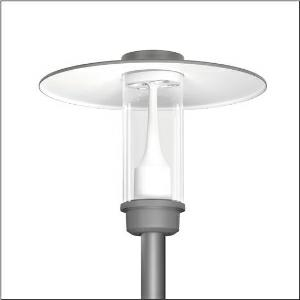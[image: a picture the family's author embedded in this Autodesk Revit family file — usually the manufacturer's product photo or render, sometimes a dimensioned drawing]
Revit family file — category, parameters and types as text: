
# Revit family: litepole_2_iq___p1_0a_5xa5425ff14h_a7e5
name_source: partatom
category: Lighting Fixtures
units: mm (PartAtom-declared; Revit-internal decimal feet)

## family parameters
Cut with Voids When Loaded = No
Host = Face
Light Source = No
Part Type = Normal
Room Calculation Point = No
Round Connector Dimension = Use Diameter
Shared = No

## types (1)
- --- (1 x LED, 1520 lm, 10.5 W, 3000K)
    Apparent Load = 11 VA
    CIE Flux Codes = 33 62 89 96 100
    Color Rendering = 70
    Color Temperature = 3000K
    Default Elevation = 1800 mm
    Description = Litepole 2 iQ, mast luminaire, Module 540 iQ-SR, primary light control with 3 zone facetted reflector, of plastic, silver coated, highly specular, structured, primary optical cover: cover, of PMMA, transparent, light distribution: P1.0a, light emission: direct distribution, primary light characteristic: strongly asymmetric, installation type: post-top, LED, High Power LED, rated luminous flux: 1.520lm, luminous efficacy: 145lm/W, light colour: 730, colour temperature: 3000K, control gear: iQ Street-Remote, control: Auto-Match, Temp-Guard, Lumen-Switch, Night-Set, Smart-Wire, Light-Fading, Desk-Remote (wireless, voltage-free reading and setting of iQ features in the workshop via application-optimized NFC function/RFID function), optimised constant luminous flux control (CLO 2.0), Street-Remote, pre-setting: logarithmic dimming characteristic, with terminal, 6-pole, max. 2.5mm², mains connection: 230..240V, AC, 50/60Hz, start of lifetime: 11W, end of service life: 11W, reduction: 5W, luminaire housing, upper part, of aluminium, coated, Siteco® metallic grey (DB 702S), diameter: 750mm, height: 590mm, spigot size: d x l = 76 x 70mm (post-top) | with reducer (optional accessory) 60 x 70mm, mounting height: 3..5m, post-top mast mounting element, of diecast aluminium, coated, Siteco® metallic grey (DB 702S), Module 540 iQ-SR, traffic white (RAL 9016), equipment: standard, protection rating (complete): IP65, insulation class (complete): insulation class II (safety insulation), certification: CE, ENEC, VDE, packaging unit: 1 piece

Light Distribution: P1.0a
    Height = 590 mm
    Lamp = 1 x LED
    Lamp Light Flux = 1520 lm
    Lamp Power = 10.5 W
    Lamp count = 1
    Length = 750 mm
    Luminous efficacy = 145 lm/W
    Manufacturer = Siteco
    ModVariant = No
    Model = 5XA5425FF14H
    Number of Poles = 1
    OnlyDefault = Yes
    Power Factor = 1
    Product Name = Litepole 2 iQ | P1.0a
    Product group = mast luminaire | pylon top
    ProductGroupID = 6100
    Protection Class = Protection class II
    Protection Degree = IP 65
    RLX_Detail_Level = 1
    RLX_Emergency_Light_Flux = 0 lm
    RLX_Emergency_Type = 0
    RLX_Emergency_Type_DB = No
    RlxData = <blob elided: 55473 chars, md5=7cb387b7>
    Socket = socket
    Standby Power = 0 W
    System Light Flux = 1520 lm
    System Power = 11 W
    Type Comments = factory setting: luminous flux: 100 % | dim-lin: 254 | 419 mA
    Type Image = l_1006518.jpg
    URL = http://relux.com
    VarID = @adj_213813
    Voltage = 0 V
    Weight = 0.00 kg
    Width = 0 mm  [stored 0 ft]

note: [stored X ft] marks values corroborated as IEEE doubles in the binary element streams (Revit-internal decimal feet)

## geometry (parser evidence)
native form markers: Blend x4, Sweep x12
no freeform markers — native parametric forms only
